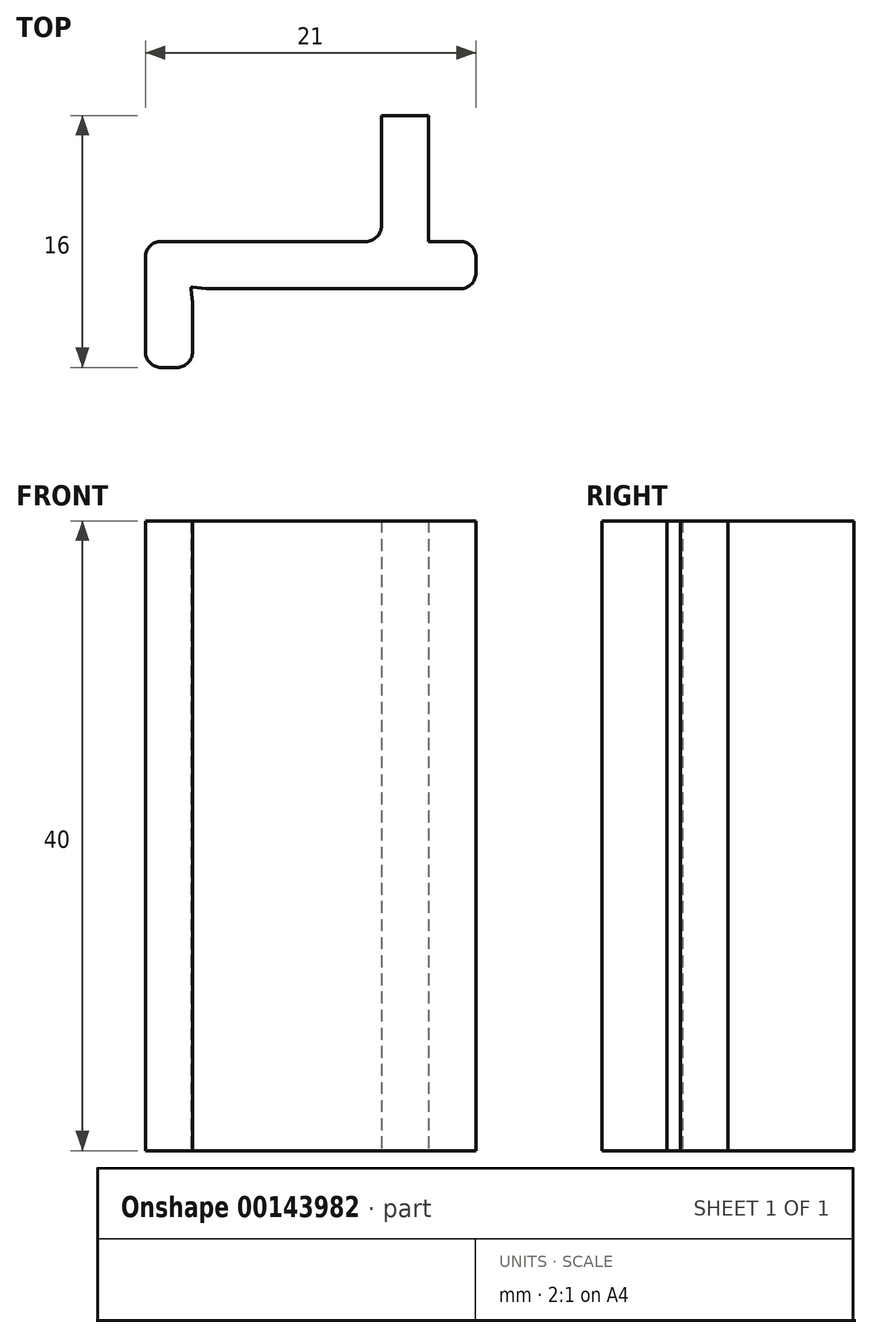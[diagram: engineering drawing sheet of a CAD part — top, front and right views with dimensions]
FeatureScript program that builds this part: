
annotation { "Feature Type Name" : "Feature", "Feature Type Description" : "" }
export const myFeature = defineFeature(function(context is Context, id is Id, definition is map)
    precondition{}
    {
        {
            var Q0;
            Q0=qCreatedBy(makeId("Top.planeOp"),FACE);
            var sketch = newSketch(context, id + "F0", { "sketchPlane" : qUnion([Q0])});
            skLineSegment(sketch, "E0", {"start": v(0, 0) * mm, "end": v(-15, 0) * mm});
            skLineSegment(sketch, "E1", {"start": v(-15, 0) * mm, "end": v(-15, -5) * mm});
            skLineSegment(sketch, "E2", {"start": v(-15, -5) * mm, "end": v(-18, -5) * mm});
            skLineSegment(sketch, "E3", {"start": v(-18, -5) * mm, "end": v(-18, 3) * mm});
            skLineSegment(sketch, "E4", {"start": v(-18, 3) * mm, "end": v(0, 3) * mm});
            skLineSegment(sketch, "E5", {"start": v(0, 3) * mm, "end": v(0, 0) * mm});
            skLineSegment(sketch, "E6", {"start": v(0, 3) * mm, "end": v(0, 11) * mm});
            skLineSegment(sketch, "E7", {"start": v(0, 11) * mm, "end": v(-3, 11) * mm});
            skLineSegment(sketch, "E8", {"start": v(-3, 11) * mm, "end": v(-3, 3) * mm});
            skCircle(sketch, "E9", {"center": v(-15, 0) * mm, "radius": 0.1 * mm});
            skLineSegment(sketch, "E10", {"start": v(-14.99, 0.1) * mm, "end": v(-14.09, 0) * mm});
            skLineSegment(sketch, "E11", {"start": v(-15.1, -0.01) * mm, "end": v(-15, -0.87) * mm});
            skLineSegment(sketch, "E12", {"start": v(0, 3) * mm, "end": v(3, 3) * mm});
            skLineSegment(sketch, "E13", {"start": v(3, 3) * mm, "end": v(3, 0) * mm});
            skLineSegment(sketch, "E14", {"start": v(3, 0) * mm, "end": v(0, 0) * mm});
            skSolve(sketch);
        }
        {
            var Q0;
            {var subQ2=sQuery(id+"F0.wireOp",EDGE,"E2");Q0=makeQuery(id+"F0.imprint","IMPRINT",FACE,{"disambiguationData":[TD([[makeQuery(id+"F0.imprint","IMPRINT",EDGE,{"derivedFrom":subQ2}),-1.0]])]});}
            var Q1;
            {var subQ0=sQuery(id+"F0.wireOp",EDGE,"E6");Q1=makeQuery(id+"F0.imprint","IMPRINT",FACE,{"disambiguationData":[TD([[makeQuery(id+"F0.imprint","IMPRINT",EDGE,{"derivedFrom":subQ0}),1.0]])]});}
            var Q2;
            Q2=makeQuery(id+"F0.imprint","IMPRINT",FACE,{"disambiguationData":[TD([[makeQuery(id+"F0.imprint","IMPRINT",EDGE,{"derivedFrom":sQuery(id+"F0.wireOp",EDGE,"E5")}),1.0]])]});
            extrude(context, id + "F1", {"entities" : qUnion([Q0, Q1, Q2]), "depth" : 40 * mm, "offsetDistance" : 25 * mm});
        }
        {
            var Q0;
            Q0=makeQuery(id+"F1.opExtrude","SWEPT_EDGE",EDGE,{"disambiguationData":[OSD([sQuery(id+"F0.wireOp",EDGE,"E0"),sQuery(id+"F0.wireOp",EDGE,"E5")])]});
            var Q1;
            Q1=makeQuery(id+"F1.opExtrude","SWEPT_EDGE",EDGE,{"disambiguationData":[OSD([sQuery(id+"F0.wireOp",EDGE,"E2"),sQuery(id+"F0.wireOp",EDGE,"E3")])]});
            var Q2;
            Q2=makeQuery(id+"F1.opExtrude","SWEPT_EDGE",EDGE,{"disambiguationData":[OSD([sQuery(id+"F0.wireOp",EDGE,"E1"),sQuery(id+"F0.wireOp",EDGE,"E2")])]});
            var Q3;
            Q3=makeQuery(id+"F1.opExtrude","SWEPT_EDGE",EDGE,{"disambiguationData":[OSD([sQuery(id+"F0.wireOp",EDGE,"E3"),sQuery(id+"F0.wireOp",EDGE,"E4")])]});
            var Q4;
            Q4=makeQuery(id+"F1.opExtrude","SWEPT_EDGE",EDGE,{"disambiguationData":[OSD([sQuery(id+"F0.wireOp",EDGE,"E13"),sQuery(id+"F0.wireOp",EDGE,"E14")])]});
            var Q5;
            Q5=makeQuery(id+"F1.opExtrude","SWEPT_EDGE",EDGE,{"disambiguationData":[OSD([sQuery(id+"F0.wireOp",EDGE,"E12"),sQuery(id+"F0.wireOp",EDGE,"E13")])]});
            var Q6;
            Q6=makeQuery(id+"F1.opExtrude","SWEPT_EDGE",EDGE,{"disambiguationData":[OSD([sQuery(id+"F0.wireOp",EDGE,"E4"),sQuery(id+"F0.wireOp",EDGE,"E8")])]});
            fillet(context, id + "F2", {"entities" : qUnion([Q0, Q1, Q2, Q3, Q4, Q5, Q6]), "radius" : 1 * mm, "tangentPropagation" : true, "allowEdgeOverflow" : false});
        }
    });
